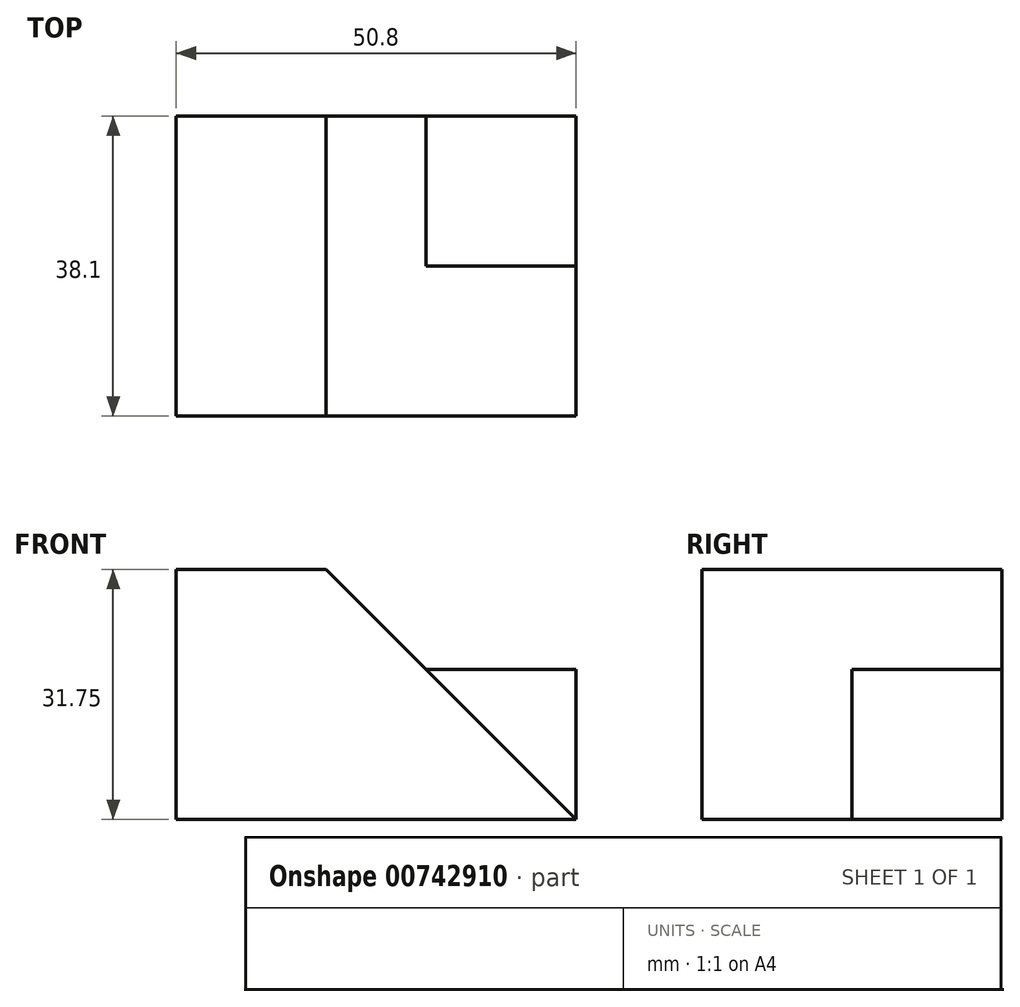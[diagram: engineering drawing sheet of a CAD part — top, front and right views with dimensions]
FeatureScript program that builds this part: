
annotation { "Feature Type Name" : "Feature", "Feature Type Description" : "" }
export const myFeature = defineFeature(function(context is Context, id is Id, definition is map)
    precondition{}
    {
        {
            var Q0;
            Q0=qCreatedBy(makeId("Front.planeOp"),FACE);
            var sketch = newSketch(context, id + "F0", { "sketchPlane" : qUnion([Q0])});
            skLineSegment(sketch, "E0", {"start": v(0, 0) * mm, "end": v(50.8, 0) * mm});
            skLineSegment(sketch, "E1", {"start": v(50.8, 0) * mm, "end": v(50.8, 31.75) * mm});
            skLineSegment(sketch, "E2", {"start": v(50.8, 31.75) * mm, "end": v(0, 31.75) * mm});
            skLineSegment(sketch, "E3", {"start": v(0, 31.75) * mm, "end": v(0, 0) * mm});
            skSolve(sketch);
        }
        {
            var Q0;
            Q0=makeQuery(id+"F0.imprint","IMPRINT",FACE,{"disambiguationData":[TD([[makeQuery(id+"F0.imprint","IMPRINT",EDGE,{"derivedFrom":sQuery(id+"F0.wireOp",EDGE,"E0")}),1.0]])]});
            extrude(context, id + "F1", {"entities" : qUnion([Q0]), "oppositeDirection" : true, "depth" : 38.1 * mm, "offsetDistance" : 25.4 * mm});
        }
        {
            var Q0;
            Q0=makeQuery(id+"F1.opExtrude","CAP_FACE",FACE,{"disambiguationData":[OSD([sQuery(id+"F0.wireOp",EDGE,"E0"),sQuery(id+"F0.wireOp",EDGE,"E1"),sQuery(id+"F0.wireOp",EDGE,"E2"),sQuery(id+"F0.wireOp",EDGE,"E3")])],"isStart":true});
            var sketch = newSketch(context, id + "F2", { "sketchPlane" : qUnion([Q0])});
            skLineSegment(sketch, "E4", {"start": v(50.8, 0) * mm, "end": v(19.05, 31.75) * mm});
            skLineSegment(sketch, "E5", {"start": v(19.05, 31.75) * mm, "end": v(50.8, 31.75) * mm});
            skLineSegment(sketch, "E6", {"start": v(50.8, 31.75) * mm, "end": v(50.8, 0) * mm});
            skSolve(sketch);
        }
        {
            var Q0;
            Q0=makeQuery(id+"F2.imprint","IMPRINT",FACE,{"disambiguationData":[TD([[makeQuery(id+"F2.imprint","IMPRINT",EDGE,{"derivedFrom":sQuery(id+"F2.wireOp",EDGE,"E4")}),-1.0]])]});
            extrude(context, id + "F3", {"entities" : qUnion([Q0]), "operationType" : NewBodyOperationType.REMOVE, "oppositeDirection" : true, "depth" : 38.1 * mm, "offsetDistance" : 25.4 * mm});
        }
        {
            var Q0;
            Q0=makeQuery(id+"F1.opExtrude","CAP_FACE",FACE,{"disambiguationData":[OSD([sQuery(id+"F0.wireOp",EDGE,"E0"),sQuery(id+"F0.wireOp",EDGE,"E1"),sQuery(id+"F0.wireOp",EDGE,"E2"),sQuery(id+"F0.wireOp",EDGE,"E3")])],"isStart":false});
            var sketch = newSketch(context, id + "F4", { "sketchPlane" : qUnion([Q0])});
            skLineSegment(sketch, "E7", {"start": v(-50.8, 0) * mm, "end": v(-50.8, 19.05) * mm});
            skLineSegment(sketch, "E8", {"start": v(-50.8, 19.05) * mm, "end": v(-31.75, 19.05) * mm});
            skLineSegment(sketch, "E9", {"start": v(-31.75, 19.05) * mm, "end": v(-50.8, 0) * mm});
            skSolve(sketch);
        }
        {
            var Q0;
            Q0=makeQuery(id+"F4.imprint","IMPRINT",FACE,{"disambiguationData":[TD([[makeQuery(id+"F4.imprint","IMPRINT",EDGE,{"derivedFrom":sQuery(id+"F4.wireOp",EDGE,"E7")}),-1.0]])]});
            extrude(context, id + "F5", {"entities" : qUnion([Q0]), "operationType" : NewBodyOperationType.ADD, "oppositeDirection" : true, "depth" : 19.05 * mm, "offsetDistance" : 25.4 * mm});
        }
    });
